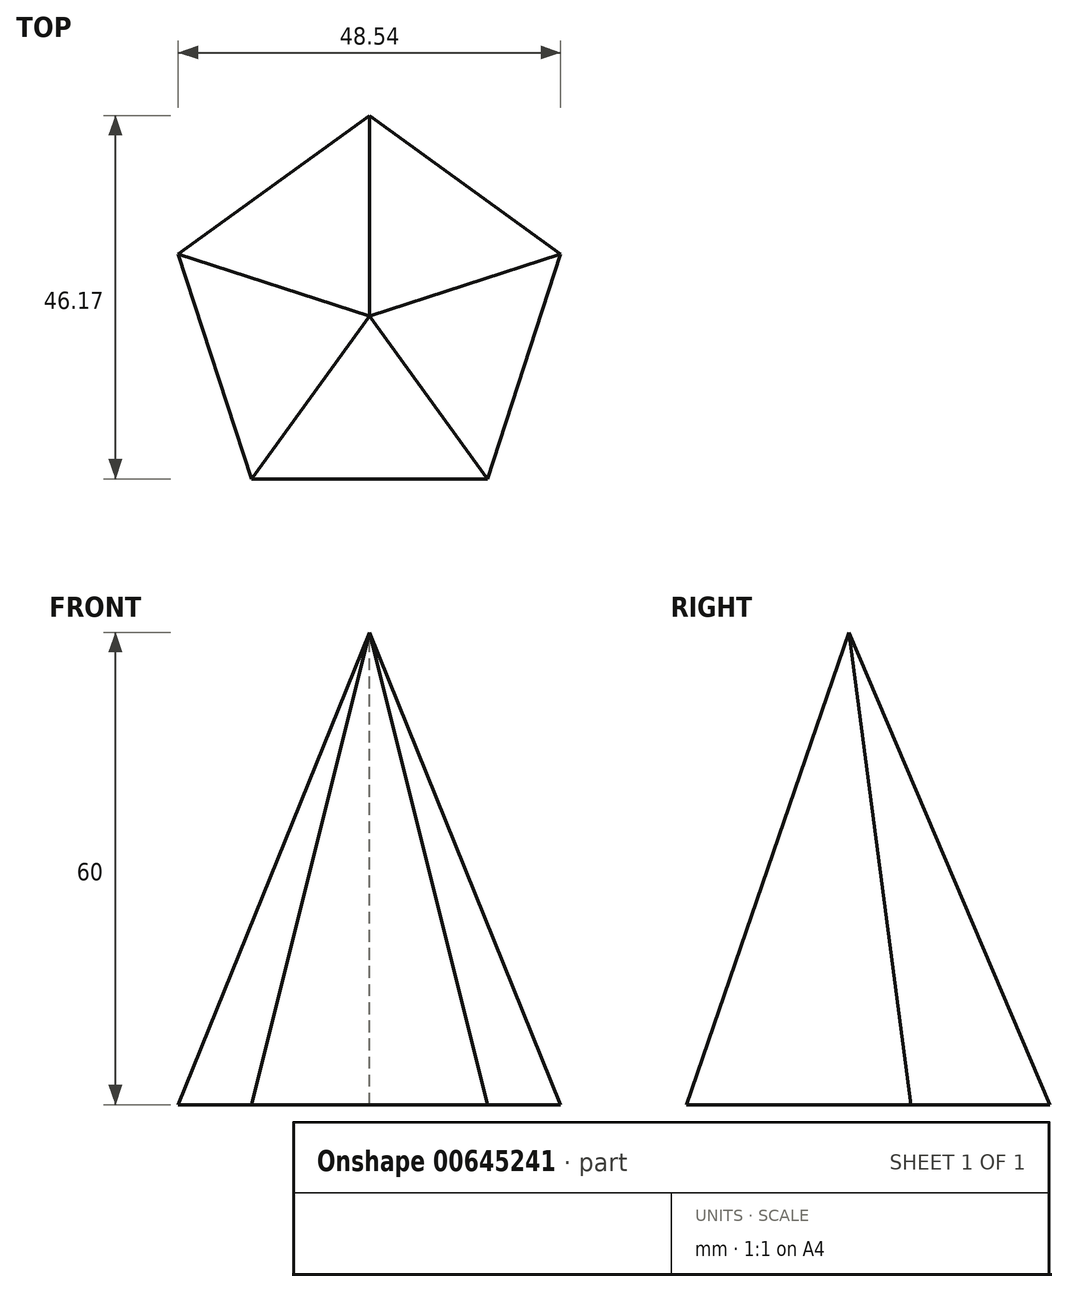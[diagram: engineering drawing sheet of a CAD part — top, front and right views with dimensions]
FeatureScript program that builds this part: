
annotation { "Feature Type Name" : "Feature", "Feature Type Description" : "" }
export const myFeature = defineFeature(function(context is Context, id is Id, definition is map)
    precondition{}
    {
        {
            var Q0;
            Q0=qCreatedBy(makeId("Top.planeOp"),FACE);
            var sketch = newSketch(context, id + "F0", { "sketchPlane" : qUnion([Q0])});
            skCircle(sketch, "E0.cCircle", {"center": v(0, 0) * mm, "radius": 20.65 * mm, "construction": true});
            skLineSegment(sketch, "E0.0", {"start": v(15, -20.65) * mm, "end": v(-15, -20.65) * mm});
            skLineSegment(sketch, "E0.1", {"start": v(-15, -20.65) * mm, "end": v(-24.27, 7.89) * mm});
            skLineSegment(sketch, "E0.2", {"start": v(-24.27, 7.89) * mm, "end": v(0, 25.52) * mm});
            skLineSegment(sketch, "E0.3", {"start": v(0, 25.52) * mm, "end": v(24.27, 7.89) * mm});
            skLineSegment(sketch, "E0.4", {"start": v(24.27, 7.89) * mm, "end": v(15, -20.65) * mm});
            skPoint(sketch, "E0.0.midPoint", {"position": v(0, -20.65) * mm});
            skSolve(sketch);
        }
        {
            var Q0;
            Q0=qCreatedBy(makeId("Right.planeOp"),FACE);
            var sketch = newSketch(context, id + "F1", { "sketchPlane" : qUnion([Q0])});
            skLineSegment(sketch, "E1", {"start": v(0, 0) * mm, "end": v(0, 60) * mm});
            skSolve(sketch);
        }
        {
            var Q0;
            Q0=makeQuery(id+"F0.imprint","IMPRINT",FACE,{"disambiguationData":[TD([[makeQuery(id+"F0.imprint","IMPRINT",EDGE,{"derivedFrom":sQuery(id+"F0.wireOp",EDGE,"E0.0")}),-1.0]])]});
            var Q1;
            Q1=sQuery(id+"F1.wireOp",VERTEX,"E1.end");
            loft(context, id + "F2", {"sheetProfilesArray" : [{ "sheetProfileEntities" : qUnion([Q0]) }, { "sheetProfileEntities" : qUnion([Q1]) }]});
        }
    });
